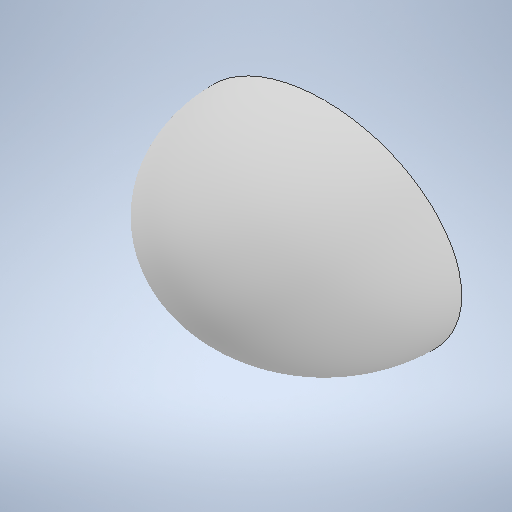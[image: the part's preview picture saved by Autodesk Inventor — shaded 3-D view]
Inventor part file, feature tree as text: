
AUTODESK INVENTOR PART (.ipt)
format: ipt  version: 2025 (Build 290162000, 162)  size: 287,232 bytes
history: native  units: mm
features: revolve x1, sketch x1
ambient origin geometry x8: Origin, YZ Plane, XZ Plane, XY Plane, X Axis, Y Axis, Z Axis, Center Point
bodies: Solid1 (feature_tree)
feature tree (2):
  revolve  "Revolution1"  [1 undecoded]
  sketch  "Sketch6"  dims[d11=180.0deg d2=0.5mm d3=0.872665mm d4=0.5mm d5=0.872665mm d9=0.872665mm d10=0.872665mm]
note: 1 required parameter value undecoded (feature->parameter linkage not recoverable at this tier; creation-order binding heuristic only, values carry confidence <= 0.55)
